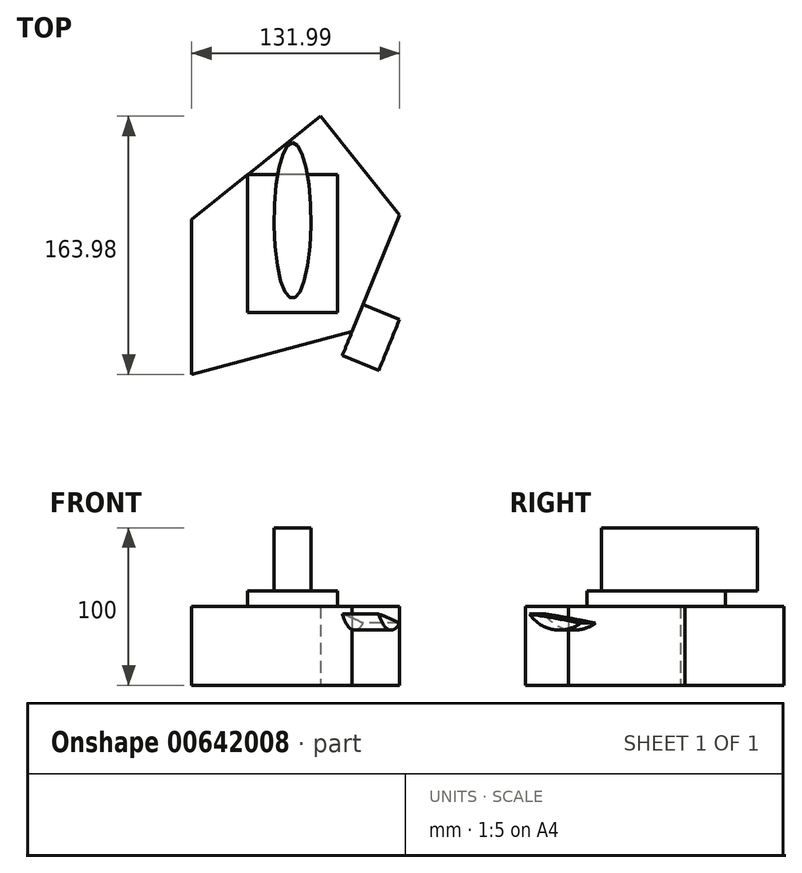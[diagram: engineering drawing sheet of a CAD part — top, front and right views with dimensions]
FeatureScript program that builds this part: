
annotation { "Feature Type Name" : "Feature", "Feature Type Description" : "" }
export const myFeature = defineFeature(function(context is Context, id is Id, definition is map)
    precondition{}
    {
        {
            var Q0;
            Q0=qCreatedBy(makeId("Top.planeOp"),FACE);
            var sketch = newSketch(context, id + "F0", { "sketchPlane" : qUnion([Q0])});
            skLineSegment(sketch, "E0", {"start": v(37.85, -37.61) * mm, "end": v(68.02, 36.46) * mm});
            skLineSegment(sketch, "E1", {"start": v(68.02, 36.46) * mm, "end": v(17.66, 99.22) * mm});
            skLineSegment(sketch, "E2", {"start": v(17.66, 99.22) * mm, "end": v(-63.97, 33.71) * mm});
            skLineSegment(sketch, "E3", {"start": v(-63.97, 33.71) * mm, "end": v(-63.97, -64.76) * mm});
            skLineSegment(sketch, "E4", {"start": v(-63.97, -64.76) * mm, "end": v(37.85, -37.61) * mm});
            skSolve(sketch);
        }
        {
            var Q0;
            Q0 = qSketchRegion(id + "F0", true);
            extrude(context, id + "F1", {"entities" : qUnion([Q0]), "depth" : 50 * mm, "offsetDistance" : 25 * mm});
        }
        {
            var Q0;
            Q0=makeQuery(id+"F1.opExtrude","CAP_FACE",FACE,{"disambiguationData":[OSD([sQuery(id+"F0.wireOp",EDGE,"E0"),sQuery(id+"F0.wireOp",EDGE,"E1"),sQuery(id+"F0.wireOp",EDGE,"E2"),sQuery(id+"F0.wireOp",EDGE,"E3"),sQuery(id+"F0.wireOp",EDGE,"E4")])],"isStart":false});
            var sketch = newSketch(context, id + "F2", { "sketchPlane" : qUnion([Q0])});
            skLineSegment(sketch, "E5.bottom", {"start": v(28.57, 62.3) * mm, "end": v(-28.57, 62.3) * mm});
            skLineSegment(sketch, "E5.top", {"start": v(28.57, -25.6) * mm, "end": v(-28.57, -25.6) * mm});
            skLineSegment(sketch, "E5.left", {"start": v(28.57, 62.3) * mm, "end": v(28.57, -25.6) * mm});
            skLineSegment(sketch, "E5.right", {"start": v(-28.57, 62.3) * mm, "end": v(-28.57, -25.6) * mm});
            skPoint(sketch, "E5.middle", {"position": v(0, 18.35) * mm});
            skSolve(sketch);
        }
        {
            var Q0;
            Q0 = qSketchRegion(id + "F2", true);
            extrude(context, id + "F3", {"entities" : qUnion([Q0]), "operationType" : NewBodyOperationType.ADD, "depth" : 10 * mm, "offsetDistance" : 25 * mm});
        }
        {
            var Q0;
            Q0=makeQuery(id+"F1.opExtrude","SWEPT_FACE",FACE,{"disambiguationData":[OSD([sQuery(id+"F0.wireOp",EDGE,"E0")])]});
            var sketch = newSketch(context, id + "F4", { "sketchPlane" : qUnion([Q0])});
            skCircle(sketch, "E6", {"center": v(12.51, 24.18) * mm, "radius": 41.93 * mm});
            skSolve(sketch);
        }
        {
            var Q0;
            Q0=makeQuery(id+"F3.opExtrude","CAP_FACE",FACE,{"disambiguationData":[OSD([sQuery(id+"F2.wireOp",EDGE,"E5.bottom"),sQuery(id+"F2.wireOp",EDGE,"E5.top"),sQuery(id+"F2.wireOp",EDGE,"E5.left"),sQuery(id+"F2.wireOp",EDGE,"E5.right")])],"isStart":false});
            var sketch = newSketch(context, id + "F5", { "sketchPlane" : qUnion([Q0])});
            skEllipse(sketch, "E7", {"center": v(0, 33) * mm, "majorRadius": 49.44 * mm, "minorRadius": 11.78 * mm, "majorAxis": v(0, 1)});
            skSolve(sketch);
        }
        {
            var Q0;
            Q0 = qSketchRegion(id + "F5", true);
            extrude(context, id + "F6", {"entities" : qUnion([Q0]), "operationType" : NewBodyOperationType.ADD, "depth" : 40 * mm, "offsetDistance" : 25 * mm});
        }
        {
            var Q0;
            Q0 = qSketchRegion(id + "F4", true);
            var sketch = newSketch(context, id + "F7", { "sketchPlane" : qUnion([Q0])});
            skArc(sketch, "E8", {"start": v(28.24, 32.95) * mm, "mid": v(-36.98, 45.29) * mm, "end": v(-103.08, 51.4) * mm});
            skArc(sketch, "E9", {"start": v(-36.98, 45.29) * mm, "mid": v(-20.66, 35.42) * mm, "end": v(-2.02, 39.47) * mm});
            skSolve(sketch);
        }
        {
            var Q0;
            Q0 = qSketchRegion(id + "F7", true);
            extrude(context, id + "F8", {"entities" : qUnion([Q0]), "operationType" : NewBodyOperationType.ADD, "depth" : 25 * mm, "offsetDistance" : 25 * mm});
        }
    });
